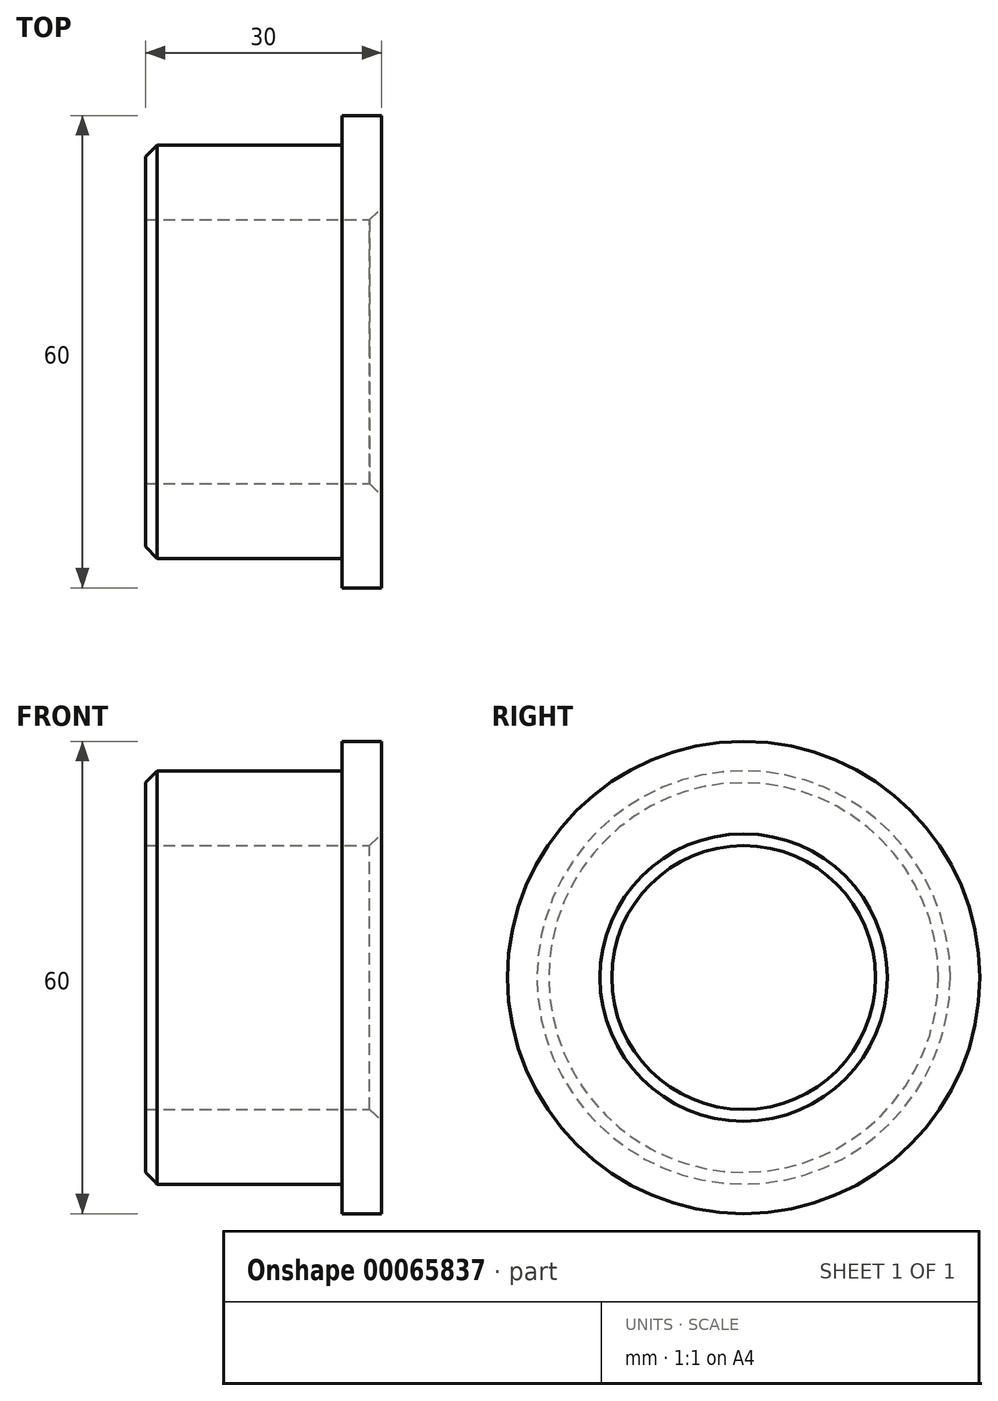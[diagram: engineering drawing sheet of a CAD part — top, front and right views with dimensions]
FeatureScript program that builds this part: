
annotation { "Feature Type Name" : "Feature", "Feature Type Description" : "" }
export const myFeature = defineFeature(function(context is Context, id is Id, definition is map)
    precondition{}
    {
        {
            var Q0;
            Q0=qCreatedBy(makeId("Front.planeOp"),FACE);
            var sketch = newSketch(context, id + "F0", { "sketchPlane" : qUnion([Q0])});
            skLineSegment(sketch, "E0", {"start": v(0, 0) * mm, "end": v(-92.6, 0) * mm, "construction": true});
            skLineSegment(sketch, "E1.bottom", {"start": v(0, 0) * mm, "end": v(30, 0) * mm});
            skLineSegment(sketch, "E1.top", {"start": v(0, 30) * mm, "end": v(30, 30) * mm});
            skLineSegment(sketch, "E1.left", {"start": v(0, 0) * mm, "end": v(0, 30) * mm});
            skLineSegment(sketch, "E1.right", {"start": v(30, 0) * mm, "end": v(30, 30) * mm});
            skLineSegment(sketch, "E2", {"start": v(0, 26.25) * mm, "end": v(25, 26.25) * mm});
            skLineSegment(sketch, "E3", {"start": v(25, 26.25) * mm, "end": v(25, 30) * mm});
            skLineSegment(sketch, "E4", {"start": v(0, 16.75) * mm, "end": v(30, 16.75) * mm});
            skSolve(sketch);
        }
        {
            var Q0;
            {var subQ0=sQuery(id+"F0.wireOp",EDGE,"E2");Q0=makeQuery(id+"F0.imprint","IMPRINT",FACE,{"disambiguationData":[TD([[makeQuery(id+"F0.imprint","IMPRINT",EDGE,{"derivedFrom":subQ0}),-1.0]])]});}
            var Q1;
            Q1=sQuery(id+"F0.wireOp",EDGE,"E0");
            revolve(context, id + "F1", {"entities" : qUnion([Q0]), "axis" : qUnion([Q1]), "revolveType" : RevolveType.FULL});
        }
        {
            var Q0;
            Q0=makeQuery(id+"F1.opRevolve","SWEPT_EDGE",EDGE,{"disambiguationData":[OSD([sQuery(id+"F0.wireOp",EDGE,"E1.left"),sQuery(id+"F0.wireOp",EDGE,"E2")])]});
            var Q1;
            Q1=makeQuery(id+"F1.opRevolve","SWEPT_EDGE",EDGE,{"disambiguationData":[OSD([sQuery(id+"F0.wireOp",EDGE,"E1.right"),sQuery(id+"F0.wireOp",EDGE,"E4")])]});
            chamfer(context, id + "F2", {"entities" : qUnion([Q0, Q1]), "width" : 1.5 * mm, "tangentPropagation" : true});
        }
    });
